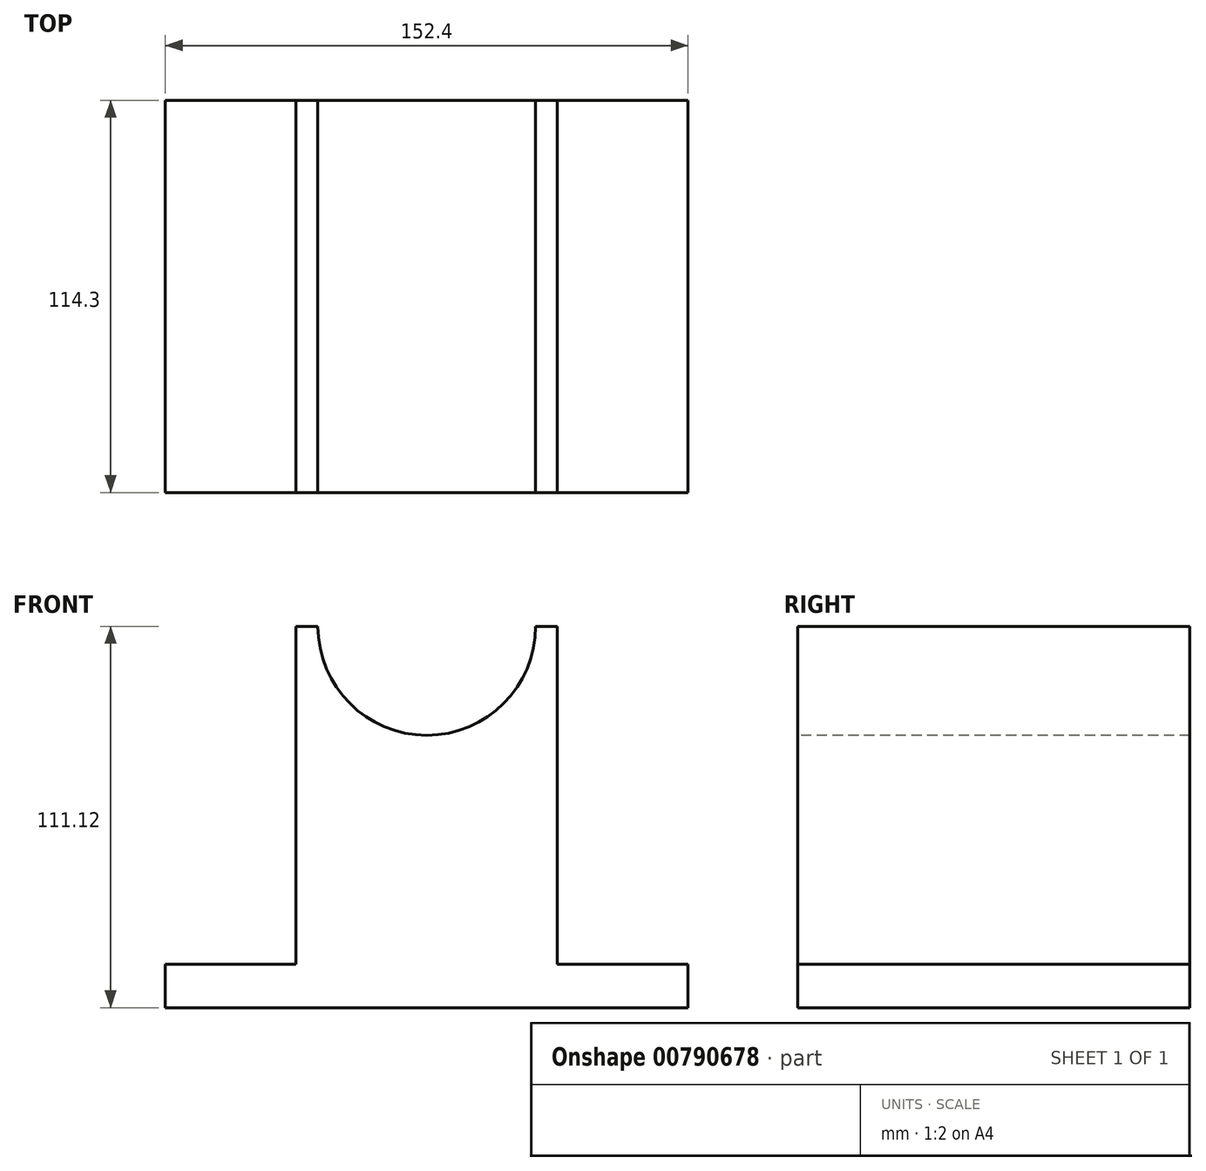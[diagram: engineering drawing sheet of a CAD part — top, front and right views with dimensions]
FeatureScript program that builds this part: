
annotation { "Feature Type Name" : "Feature", "Feature Type Description" : "" }
export const myFeature = defineFeature(function(context is Context, id is Id, definition is map)
    precondition{}
    {
        {
            var Q0;
            Q0=qCreatedBy(makeId("Front.planeOp"),FACE);
            var sketch = newSketch(context, id + "F0", { "sketchPlane" : qUnion([Q0])});
            skLineSegment(sketch, "E0", {"start": v(0, 0) * mm, "end": v(152.4, 0) * mm});
            skLineSegment(sketch, "E1", {"start": v(152.4, 0) * mm, "end": v(152.4, 12.7) * mm});
            skLineSegment(sketch, "E2", {"start": v(114.3, 12.7) * mm, "end": v(114.3, 111.12) * mm});
            skLineSegment(sketch, "E3", {"start": v(114.3, 111.12) * mm, "end": v(38.1, 111.12) * mm});
            skLineSegment(sketch, "E4", {"start": v(38.1, 111.12) * mm, "end": v(38.1, 12.7) * mm});
            skLineSegment(sketch, "E5", {"start": v(38.1, 12.7) * mm, "end": v(0, 12.7) * mm});
            skLineSegment(sketch, "E6", {"start": v(114.3, 12.7) * mm, "end": v(152.4, 12.7) * mm});
            skLineSegment(sketch, "E7", {"start": v(0, 12.7) * mm, "end": v(0, 0) * mm});
            skSolve(sketch);
        }
        {
            var Q0;
            Q0=makeQuery(id+"F0.imprint","IMPRINT",FACE,{"disambiguationData":[TD([[makeQuery(id+"F0.imprint","IMPRINT",EDGE,{"derivedFrom":sQuery(id+"F0.wireOp",EDGE,"E0")}),1.0]])]});
            extrude(context, id + "F1", {"entities" : qUnion([Q0]), "depth" : 114.3 * mm, "offsetDistance" : 25.4 * mm});
        }
        {
            var Q0;
            Q0=makeQuery(id+"F1.opExtrude","CAP_FACE",FACE,{"disambiguationData":[OSD([sQuery(id+"F0.wireOp",EDGE,"E0"),sQuery(id+"F0.wireOp",EDGE,"E1"),sQuery(id+"F0.wireOp",EDGE,"E2"),sQuery(id+"F0.wireOp",EDGE,"E3"),sQuery(id+"F0.wireOp",EDGE,"E4"),sQuery(id+"F0.wireOp",EDGE,"E5"),sQuery(id+"F0.wireOp",EDGE,"E6"),sQuery(id+"F0.wireOp",EDGE,"E7")])],"isStart":false});
            var sketch = newSketch(context, id + "F2", { "sketchPlane" : qUnion([Q0])});
            skLineSegment(sketch, "E8", {"start": v(38.1, 111.12) * mm, "end": v(44.45, 111.12) * mm});
            skLineSegment(sketch, "E9", {"start": v(114.3, 111.12) * mm, "end": v(107.95, 111.12) * mm});
            skLineSegment(sketch, "E10", {"start": v(44.45, 111.12) * mm, "end": v(76.2, 111.12) * mm});
            skLineSegment(sketch, "E11", {"start": v(76.2, 111.12) * mm, "end": v(107.95, 111.13) * mm});
            skArc(sketch, "E12", {"start": v(44.45, 111.12) * mm, "mid": v(76.2, 79.37) * mm, "end": v(107.95, 111.12) * mm});
            skSolve(sketch);
        }
        {
            var Q0;
            Q0 = qSketchRegion(id + "F2", true);
            extrude(context, id + "F3", {"entities" : qUnion([Q0]), "operationType" : NewBodyOperationType.REMOVE, "oppositeDirection" : true, "depth" : 114.3 * mm, "offsetDistance" : 25.4 * mm});
        }
    });
